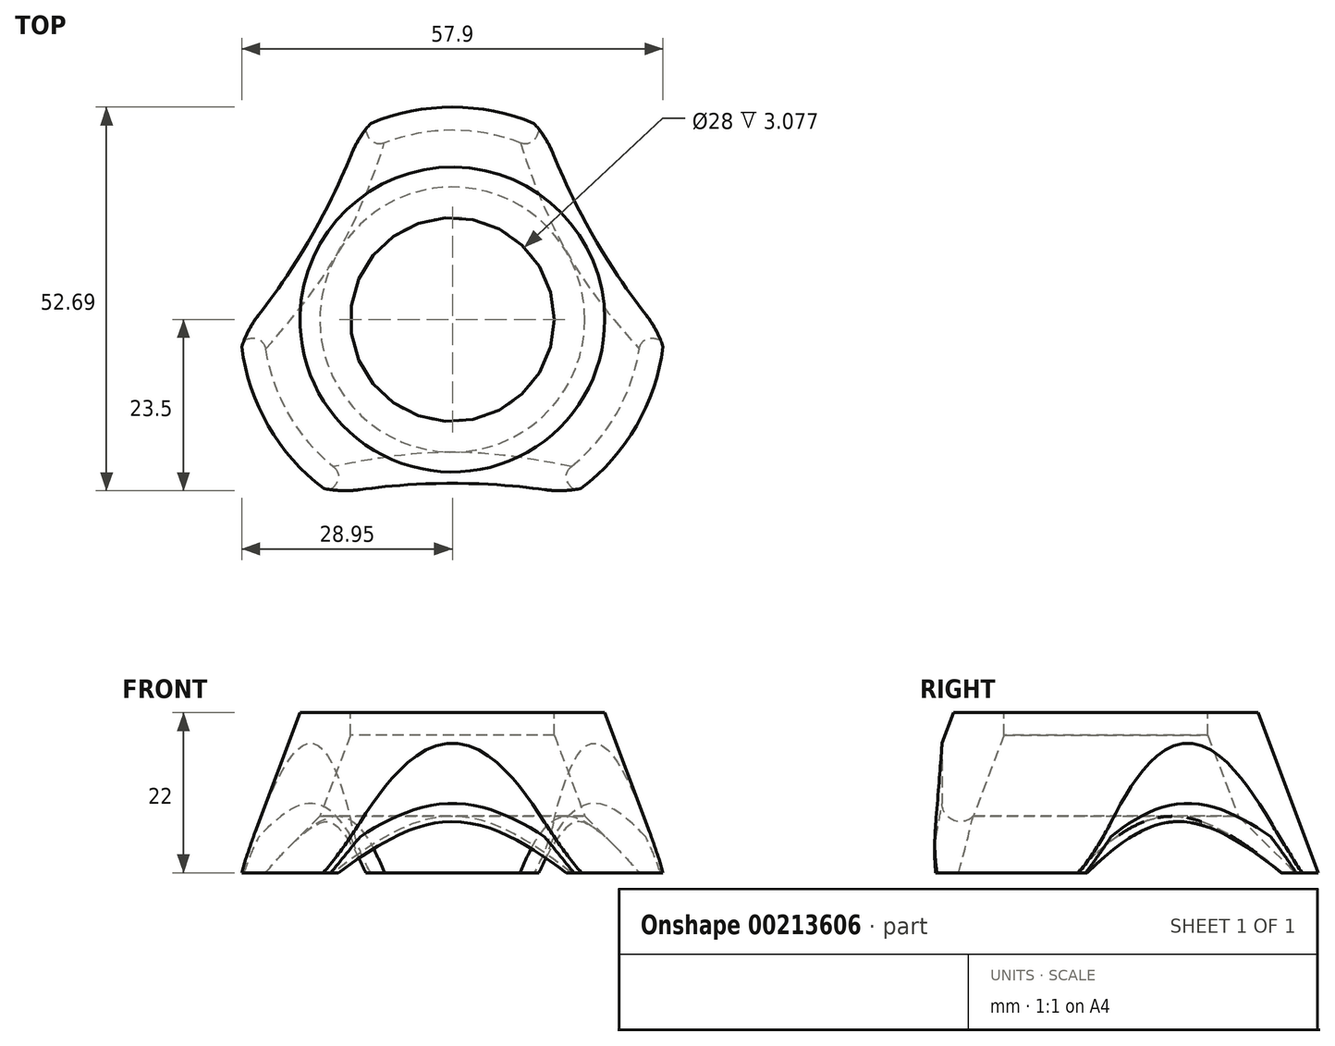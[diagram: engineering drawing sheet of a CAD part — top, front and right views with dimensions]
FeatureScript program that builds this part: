
annotation { "Feature Type Name" : "Feature", "Feature Type Description" : "" }
export const myFeature = defineFeature(function(context is Context, id is Id, definition is map)
    precondition{}
    {
        {
            var Q0;
            Q0=qCreatedBy(makeId("Top.planeOp"),FACE);
            var sketch = newSketch(context, id + "F0", { "sketchPlane" : qUnion([Q0])});
            skLineSegment(sketch, "E0", {"start": v(0, 0) * mm, "end": v(-39.83, -23) * mm, "construction": true});
            skLineSegment(sketch, "E1", {"start": v(0, 0) * mm, "end": v(48.1, -27.78) * mm, "construction": true});
            skArc(sketch, "E2", {"start": v(12.7, -23.36) * mm, "mid": v(27.71, -16) * mm, "end": v(26.58, 0.69) * mm});
            skArc(sketch, "E3", {"start": v(13.89, 22.67) * mm, "mid": v(0, 32) * mm, "end": v(-13.89, 22.67) * mm});
            skArc(sketch, "E4", {"start": v(-26.58, 0.69) * mm, "mid": v(-19.49, 11.25) * mm, "end": v(-13.89, 22.67) * mm});
            skArc(sketch, "E5", {"start": v(13.89, 22.67) * mm, "mid": v(19.49, 11.25) * mm, "end": v(26.58, 0.69) * mm});
            skCircle(sketch, "E6", {"center": v(0, 0) * mm, "radius": 22.5 * mm, "construction": true});
            skArc(sketch, "E7", {"start": v(-26.58, 0.69) * mm, "mid": v(-27.71, -16) * mm, "end": v(-12.7, -23.36) * mm});
            skArc(sketch, "E8", {"start": v(12.7, -23.36) * mm, "mid": v(0, -22.5) * mm, "end": v(-12.7, -23.36) * mm});
            skCircle(sketch, "E9", {"center": v(0, 0) * mm, "radius": 32 * mm, "construction": true});
            skSolve(sketch);
        }
        {
            var Q0;
            Q0 = qSketchRegion(id + "F0", true);
            extrude(context, id + "F1", {"entities" : qUnion([Q0]), "depth" : 22 * mm});
        }
        {
            var Q0;
            Q0=qCreatedBy(makeId("Right.planeOp"),FACE);
            var sketch = newSketch(context, id + "F2", { "sketchPlane" : qUnion([Q0])});
            skLineSegment(sketch, "E10", {"start": v(0, 0) * mm, "end": v(0, 40.32) * mm, "construction": true});
            skLineSegment(sketch, "E11", {"start": v(22, 32.93) * mm, "end": v(22, -20.48) * mm, "construction": true});
            skLineSegment(sketch, "E12", {"start": v(22, 3) * mm, "end": v(-12.68, 3) * mm, "construction": true});
            skLineSegment(sketch, "E13", {"start": v(20, 28.07) * mm, "end": v(20, -6.24) * mm, "construction": true});
            skLineSegment(sketch, "E14", {"start": v(-28.35, 23) * mm, "end": v(25.46, 23) * mm, "construction": true});
            skLineSegment(sketch, "E15", {"start": v(12.5, 22) * mm, "end": v(12.5, 5.32) * mm, "construction": true});
            skLineSegment(sketch, "E16", {"start": v(0, 0) * mm, "end": v(26, 0) * mm});
            skLineSegment(sketch, "E17", {"start": v(26, 0) * mm, "end": v(18.2, 7.8) * mm});
            skLineSegment(sketch, "E18", {"start": v(0, 23) * mm, "end": v(0, 0) * mm});
            skLineSegment(sketch, "E19", {"start": v(14, 22) * mm, "end": v(0, 22) * mm});
            skLineSegment(sketch, "E20", {"start": v(0, 22) * mm, "end": v(0, 0) * mm});
            skLineSegment(sketch, "E21", {"start": v(14, 22) * mm, "end": v(14, 18.92) * mm});
            skLineSegment(sketch, "E22", {"start": v(14, 18.92) * mm, "end": v(18.2, 7.8) * mm});
            skSolve(sketch);
        }
        {
            var Q0;
            Q0=makeQuery(id+"F2.imprint","IMPRINT",FACE,{"disambiguationData":[TD([[makeQuery(id+"F2.imprint","IMPRINT",EDGE,{"derivedFrom":sQuery(id+"F2.wireOp",EDGE,"E16")}),1.0]])]});
            var Q1;
            Q1=sQuery(id+"F2.wireOp",EDGE,"E10");
            revolve(context, id + "F3", {"operationType" : NewBodyOperationType.REMOVE, "entities" : qUnion([Q0]), "axis" : qUnion([Q1]), "revolveType" : RevolveType.FULL, "oppositeDirection" : true});
        }
        {
            var Q0;
            Q0=qCreatedBy(makeId("Right.planeOp"),FACE);
            var sketch = newSketch(context, id + "F4", { "sketchPlane" : qUnion([Q0])});
            skLineSegment(sketch, "E23", {"start": v(32, -7.5) * mm, "end": v(40.57, -30.35) * mm, "construction": true});
            skLineSegment(sketch, "E24", {"start": v(0, 0) * mm, "end": v(0, 43.62) * mm, "construction": true});
            skLineSegment(sketch, "E25", {"start": v(32, -7.5) * mm, "end": v(32, 22) * mm});
            skLineSegment(sketch, "E26", {"start": v(32, 22) * mm, "end": v(20.94, 22) * mm});
            skLineSegment(sketch, "E27", {"start": v(20.94, 22) * mm, "end": v(32, -7.5) * mm});
            skLineSegment(sketch, "E28", {"start": v(28.75, 40.13) * mm, "end": v(28.75, -14.92) * mm, "construction": true});
            skSolve(sketch);
        }
        {
            var Q0;
            Q0 = qSketchRegion(id + "F4", true);
            var Q1;
            Q1=sQuery(id+"F4.wireOp",EDGE,"E24");
            revolve(context, id + "F5", {"operationType" : NewBodyOperationType.REMOVE, "entities" : qUnion([Q0]), "axis" : qUnion([Q1]), "revolveType" : RevolveType.FULL, "oppositeDirection" : true});
        }
        {
            var Q0;
            Q0=makeQuery(id+"F3.boolean.opBoolean","INTERSECT",EDGE,{"derivedFrom":[makeQuery(id+"F1.opExtrude","SWEPT_FACE",FACE,{"disambiguationData":[OSD([sQuery(id+"F0.wireOp",EDGE,"E8")])]}),makeQuery(id+"F3.opRevolve","SWEPT_FACE",FACE,{"disambiguationData":[OSD([sQuery(id+"F2.wireOp",EDGE,"E17")])]})]});
            var Q1;
            Q1=makeQuery(id+"F3.boolean.opBoolean","INTERSECT",EDGE,{"derivedFrom":[makeQuery(id+"F1.opExtrude","SWEPT_FACE",FACE,{"disambiguationData":[OSD([sQuery(id+"F0.wireOp",EDGE,"E4")])]}),makeQuery(id+"F3.opRevolve","SWEPT_FACE",FACE,{"disambiguationData":[OSD([sQuery(id+"F2.wireOp",EDGE,"E17")])]})]});
            var Q2;
            Q2=makeQuery(id+"F3.boolean.opBoolean","INTERSECT",EDGE,{"derivedFrom":[makeQuery(id+"F1.opExtrude","SWEPT_FACE",FACE,{"disambiguationData":[OSD([sQuery(id+"F0.wireOp",EDGE,"E5")])]}),makeQuery(id+"F3.opRevolve","SWEPT_FACE",FACE,{"disambiguationData":[OSD([sQuery(id+"F2.wireOp",EDGE,"E17")])]})]});
            fillet(context, id + "F6", {"entities" : qUnion([Q0, Q1, Q2]), "radius" : 2.5 * mm, "tangentPropagation" : true, "allowEdgeOverflow" : false});
        }
    });
